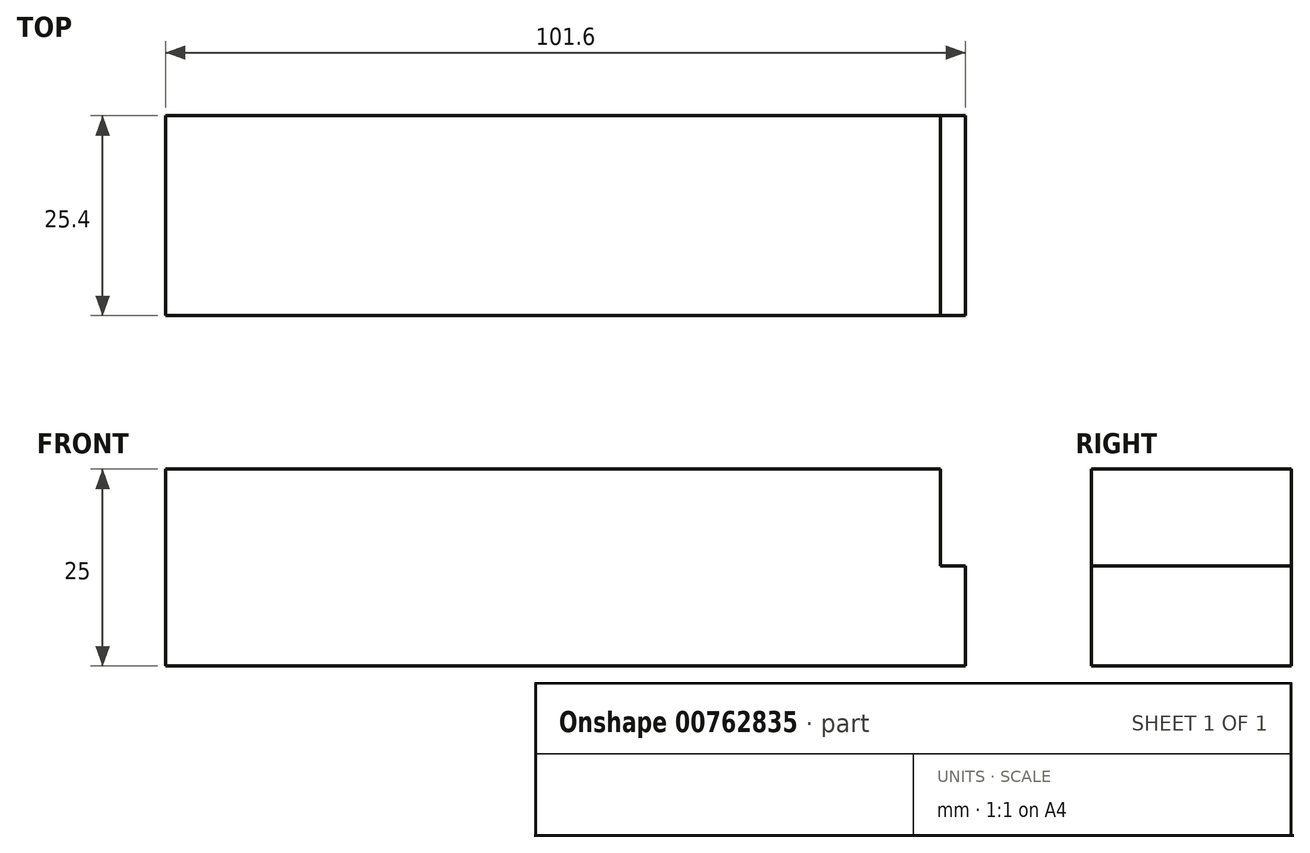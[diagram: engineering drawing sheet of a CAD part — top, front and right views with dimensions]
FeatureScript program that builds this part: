
annotation { "Feature Type Name" : "Feature", "Feature Type Description" : "" }
export const myFeature = defineFeature(function(context is Context, id is Id, definition is map)
    precondition{}
    {
        {
            var Q0;
            Q0=qCreatedBy(makeId("Top.planeOp"),FACE);
            var sketch = newSketch(context, id + "F0", { "sketchPlane" : qUnion([Q0])});
            skLineSegment(sketch, "E0.bottom", {"start": v(0, 0) * mm, "end": v(101.6, 0) * mm});
            skLineSegment(sketch, "E0.top", {"start": v(0, -25.4) * mm, "end": v(101.6, -25.4) * mm});
            skLineSegment(sketch, "E0.left", {"start": v(0, 0) * mm, "end": v(0, -25.4) * mm});
            skLineSegment(sketch, "E0.right", {"start": v(101.6, 0) * mm, "end": v(101.6, -25.4) * mm});
            skLineSegment(sketch, "E1.bottom", {"start": v(0, 0) * mm, "end": v(98.42, 0) * mm});
            skLineSegment(sketch, "E1.top", {"start": v(0, -25.4) * mm, "end": v(98.42, -25.4) * mm});
            skLineSegment(sketch, "E1.right", {"start": v(98.42, 0) * mm, "end": v(98.42, -25.4) * mm});
            skSolve(sketch);
        }
        {
            var Q0;
            {var subQ0=sQuery(id+"F0.wireOp",EDGE,"E0.left");Q0=makeQuery(id+"F0.imprint","IMPRINT",FACE,{"disambiguationData":[TD([[makeQuery(id+"F0.imprint","IMPRINT",EDGE,{"derivedFrom":subQ0}),1.0]])]});}
            extrude(context, id + "F1", {"entities" : qUnion([Q0]), "depth" : 25 * mm, "offsetDistance" : 25 * mm});
        }
        {
            var Q0;
            {var subQ0=sQuery(id+"F0.wireOp",EDGE,"E0.right");Q0=makeQuery(id+"F0.imprint","IMPRINT",FACE,{"disambiguationData":[TD([[makeQuery(id+"F0.imprint","IMPRINT",EDGE,{"derivedFrom":subQ0}),-1.0]])]});}
            extrude(context, id + "F2", {"entities" : qUnion([Q0]), "operationType" : NewBodyOperationType.ADD, "depth" : 12.7 * mm, "offsetDistance" : 25 * mm});
        }
    });
